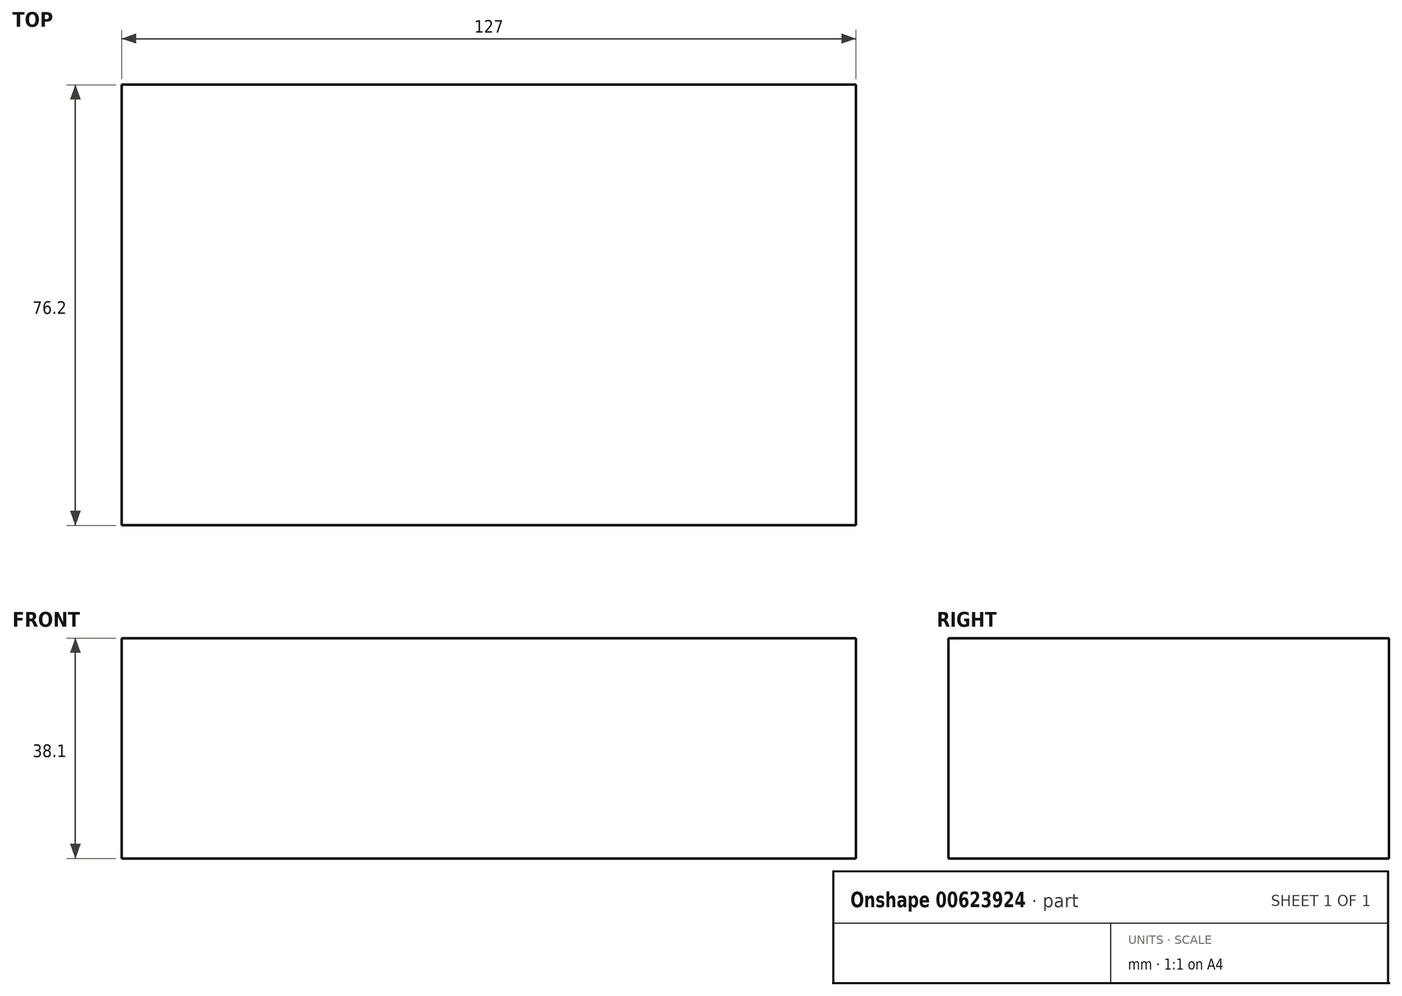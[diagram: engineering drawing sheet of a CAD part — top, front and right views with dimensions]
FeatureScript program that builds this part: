
annotation { "Feature Type Name" : "Feature", "Feature Type Description" : "" }
export const myFeature = defineFeature(function(context is Context, id is Id, definition is map)
    precondition{}
    {
        {
            var Q0;
            Q0=qCreatedBy(makeId("Top.planeOp"),FACE);
            var sketch = newSketch(context, id + "F0", { "sketchPlane" : qUnion([Q0])});
            skLineSegment(sketch, "E0.bottom", {"start": v(-121.75, 10.18) * mm, "end": v(5.25, 10.18) * mm});
            skLineSegment(sketch, "E0.top", {"start": v(-121.75, -66.02) * mm, "end": v(5.25, -66.02) * mm});
            skLineSegment(sketch, "E0.left", {"start": v(-121.75, 10.18) * mm, "end": v(-121.75, -66.02) * mm});
            skLineSegment(sketch, "E0.right", {"start": v(5.25, 10.18) * mm, "end": v(5.25, -66.02) * mm});
            skSolve(sketch);
        }
        {
            var Q0;
            Q0 = qSketchRegion(id + "F0", true);
            extrude(context, id + "F1", {"entities" : qUnion([Q0]), "depth" : 38.1 * mm, "offsetDistance" : 25.4 * mm});
        }
    });
